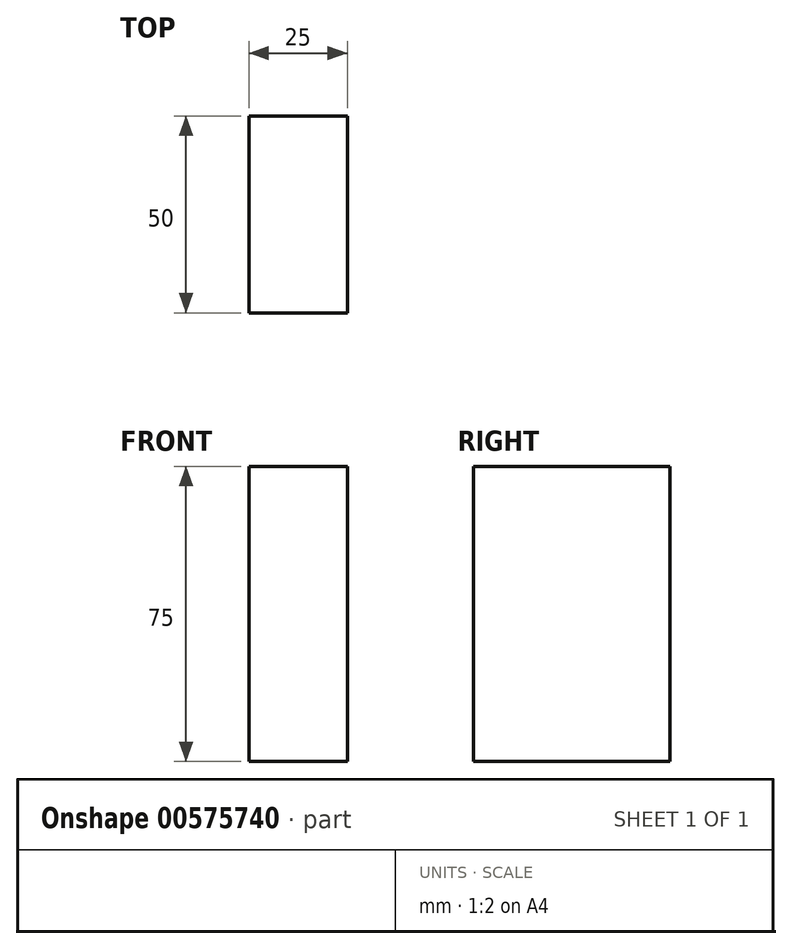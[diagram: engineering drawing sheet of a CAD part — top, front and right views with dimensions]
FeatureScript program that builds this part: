
annotation { "Feature Type Name" : "Feature", "Feature Type Description" : "" }
export const myFeature = defineFeature(function(context is Context, id is Id, definition is map)
    precondition{}
    {
        {
            var Q0;
            Q0=qCreatedBy(makeId("Top.planeOp"),FACE);
            var sketch = newSketch(context, id + "F0", { "sketchPlane" : qUnion([Q0])});
            skLineSegment(sketch, "E0.bottom", {"start": v(0, 0) * mm, "end": v(-25, 0) * mm});
            skLineSegment(sketch, "E0.top", {"start": v(0, 50) * mm, "end": v(-25, 50) * mm});
            skLineSegment(sketch, "E0.left", {"start": v(0, 0) * mm, "end": v(0, 50) * mm});
            skLineSegment(sketch, "E0.right", {"start": v(-25, 0) * mm, "end": v(-25, 50) * mm});
            skSolve(sketch);
        }
        {
            var Q0;
            Q0 = qSketchRegion(id + "F0", true);
            extrude(context, id + "F1", {"entities" : qUnion([Q0]), "depth" : 75 * mm, "offsetDistance" : 25 * mm});
        }
    });
